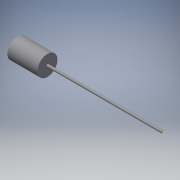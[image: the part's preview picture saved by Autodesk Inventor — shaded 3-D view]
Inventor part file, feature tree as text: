
AUTODESK INVENTOR PART (.ipt)
format: ipt  version: 2018 (Build 220112000, 112)  size: 100,352 bytes
history: native  units: in
note: dims shown in document units (in); Inventor stores cm internally (conversion verified against a paired STEP export)
features: revolve x1, other x1, sketch x1
ambient origin geometry x8: Origin, YZ Plane, XZ Plane, XY Plane, X Axis, Y Axis, Z Axis, Center Point
bodies: Solid1 (feature_tree)
feature tree (3):
  revolve  "Revolution1"  [1 undecoded]
  other  "Work Point1"
  sketch  "Sketch1"  dims[d0=0.125in d1=11.5in d2=1.0in d3=3.0in d4=90.0deg]
note: 1 required parameter value undecoded (feature->parameter linkage not recoverable at this tier; creation-order binding heuristic only, values carry confidence <= 0.55)
